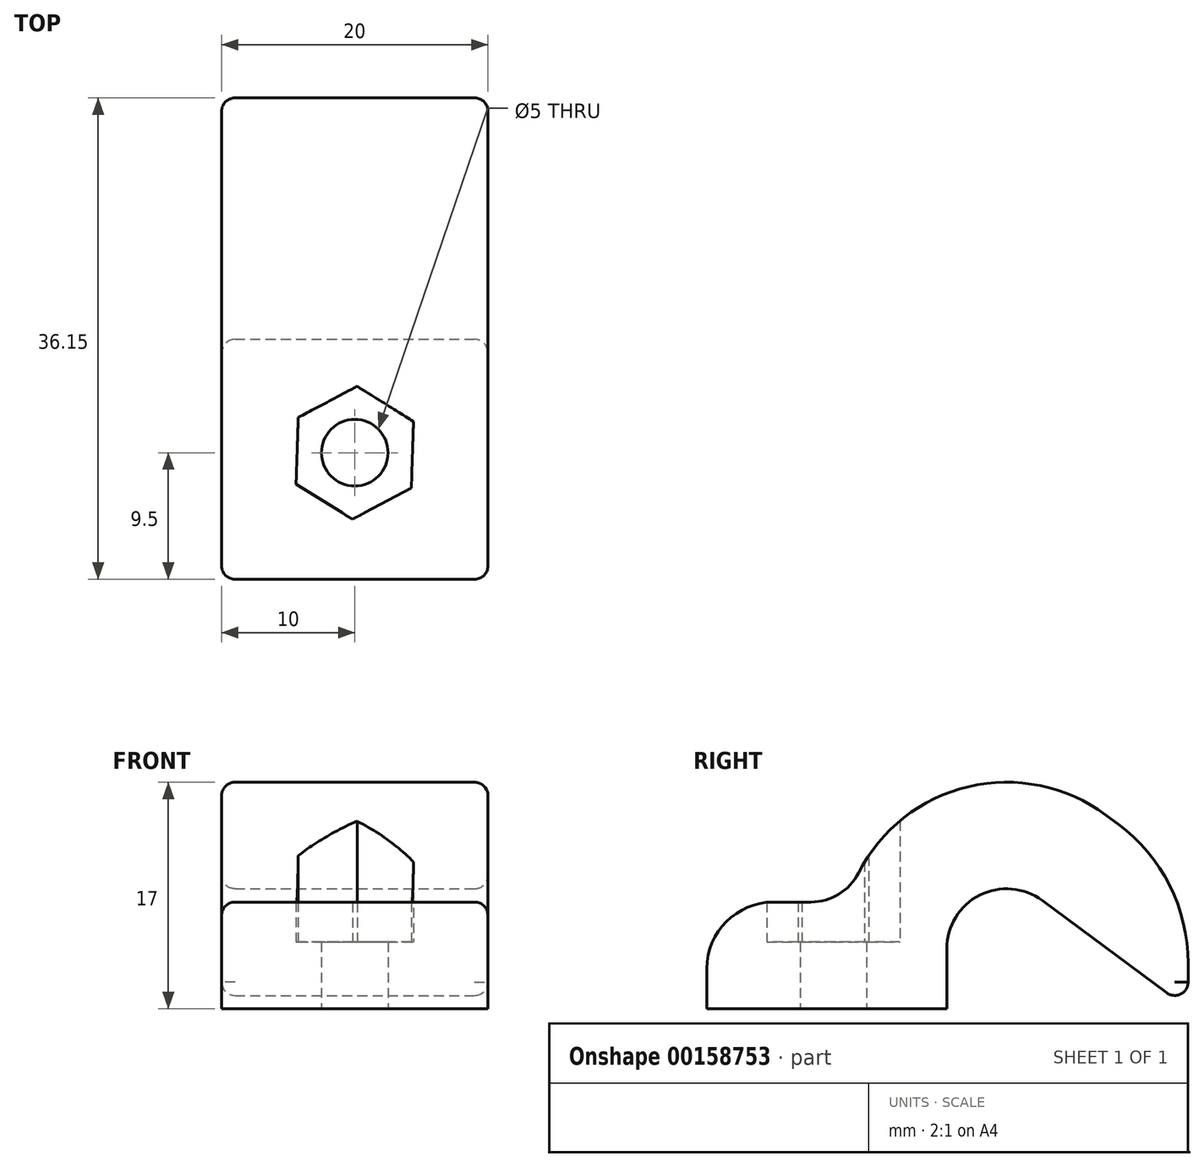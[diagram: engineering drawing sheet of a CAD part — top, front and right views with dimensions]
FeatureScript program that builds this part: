
annotation { "Feature Type Name" : "Feature", "Feature Type Description" : "" }
export const myFeature = defineFeature(function(context is Context, id is Id, definition is map)
    precondition{}
    {
        {
            var Q0;
            Q0=qCreatedBy(makeId("Front.planeOp"),FACE);
            var sketch = newSketch(context, id + "F0", { "sketchPlane" : qUnion([Q0])});
            skArc(sketch, "E0", {"start": v(-18.02, 4.5) * mm, "mid": v(-20.5, 8.52) * mm, "end": v(-25.2, 8.12) * mm});
            skPoint(sketch, "E0.first.point", {"position": v(-22.52, 0) * mm});
            skPoint(sketch, "E0.second.point", {"position": v(-22.52, 9) * mm});
            skPoint(sketch, "E0.third.point", {"position": v(-26.45, 6.68) * mm});
            skLineSegment(sketch, "E1", {"start": v(-36.15, 0) * mm, "end": v(-25.2, 8.12) * mm});
            skLineSegment(sketch, "E2", {"start": v(-18.02, 0) * mm, "end": v(-18.02, 4.5) * mm});
            skLineSegment(sketch, "E3", {"start": v(0, 8) * mm, "end": v(-10.52, 8) * mm});
            skLineSegment(sketch, "E4", {"start": v(-36.15, 9.96) * mm, "end": v(-36.15, 0) * mm});
            skLineSegment(sketch, "E5", {"start": v(0, 8) * mm, "end": v(0, 0) * mm});
            skLineSegment(sketch, "E6", {"start": v(0, 0) * mm, "end": v(-18.02, 0) * mm});
            skPoint(sketch, "E7.start.orphan", {"position": v(0, 16.03) * mm});
            skPoint(sketch, "E8.start.orphan", {"position": v(-36.15, 16.17) * mm});
            skArc(sketch, "E9.1", {"start": v(-10.52, 8) * mm, "mid": v(-18.53, 16.35) * mm, "end": v(-29.96, 14.54) * mm});
            skLineSegment(sketch, "E9.2", {"start": v(-36.15, 9.96) * mm, "end": v(-29.96, 14.54) * mm});
            skPoint(sketch, "E9.0.start.orphan", {"position": v(-10.52, 0) * mm});
            skSolve(sketch);
        }
        {
            var Q0;
            Q0 = qSketchRegion(id + "F0", true);
            extrude(context, id + "F1", {"entities" : qUnion([Q0]), "endBound" : BoundingType.SYMMETRIC, "depth" : 20 * mm});
        }
        {
            var Q0;
            Q0=makeQuery(id+"F1.opExtrude","SWEPT_EDGE",EDGE,{"disambiguationData":[OSD([sQuery(id+"F0.wireOp",EDGE,"E4"),sQuery(id+"F0.wireOp",EDGE,"E9.2")])]});
            fillet(context, id + "F2", {"entities" : qUnion([Q0]), "radius" : 13 * mm, "tangentPropagation" : true, "allowEdgeOverflow" : false});
        }
        {
            var Q0;
            Q0=makeQuery(id+"F1.opExtrude","SWEPT_EDGE",EDGE,{"disambiguationData":[OSD([sQuery(id+"F0.wireOp",EDGE,"E3"),sQuery(id+"F0.wireOp",EDGE,"E9.1")])]});
            fillet(context, id + "F3", {"entities" : qUnion([Q0]), "radius" : 4 * mm, "tangentPropagation" : true, "allowEdgeOverflow" : false});
        }
        {
            var Q0;
            Q0=makeQuery(id+"F1.opExtrude","SWEPT_EDGE",EDGE,{"disambiguationData":[OSD([sQuery(id+"F0.wireOp",EDGE,"E3"),sQuery(id+"F0.wireOp",EDGE,"E5")])]});
            fillet(context, id + "F4", {"entities" : qUnion([Q0]), "radius" : 5 * mm, "tangentPropagation" : true, "allowEdgeOverflow" : false});
        }
        {
            var Q0;
            Q0=makeQuery(id+"F1.opExtrude","SWEPT_FACE",FACE,{"disambiguationData":[OSD([sQuery(id+"F0.wireOp",EDGE,"E6")])]});
            var sketch = newSketch(context, id + "F5", { "sketchPlane" : qUnion([Q0])});
            skCircle(sketch, "E10", {"center": v(-9.5, 0) * mm, "radius": 2.5 * mm});
            skSolve(sketch);
        }
        {
            var Q0;
            Q0 = qSketchRegion(id + "F5", true);
            extrude(context, id + "F6", {"entities" : qUnion([Q0]), "operationType" : NewBodyOperationType.REMOVE, "oppositeDirection" : true, "depth" : 25 * mm});
        }
        {
            var Q0;
            Q0=qCreatedBy(makeId("Top.planeOp"),FACE);
            cPlane(context, id + "F7", {"entities" : qUnion([Q0]), "cplaneType" : CPlaneType.OFFSET, "offset" : 5 * mm, "width" : 150 * mm, "height" : 150 * mm});
        }
        {
            var Q0;
            Q0=makeQuery(id+"F1.opExtrude","SWEPT_BODY",BODY,{"disambiguationData":[OSD([sQuery(id+"F0.wireOp",EDGE,"E0"),sQuery(id+"F0.wireOp",EDGE,"E1"),sQuery(id+"F0.wireOp",EDGE,"E2"),sQuery(id+"F0.wireOp",EDGE,"E3"),sQuery(id+"F0.wireOp",EDGE,"E4"),sQuery(id+"F0.wireOp",EDGE,"E5"),sQuery(id+"F0.wireOp",EDGE,"E6"),sQuery(id+"F0.wireOp",EDGE,"E9.1"),sQuery(id+"F0.wireOp",EDGE,"E9.2")])]});
            var Q1;
            Q1=makeQuery(id+"F1.opExtrude","CAP_EDGE",EDGE,{"disambiguationData":[OSD([sQuery(id+"F0.wireOp",EDGE,"E5")])],"isStart":false});
            transform(context, id + "F8", {"entities" : qUnion([Q0]), "transformType" : TransformType.ROTATION, "transformAxis" : qUnion([Q1]), "angle" : 90 * degree, "makeCopy" : false});
        }
        {
            var Q0;
            Q0=qCreatedBy(id+"F7.planeOp",FACE);
            var sketch = newSketch(context, id + "F9", { "sketchPlane" : qUnion([Q0])});
            skCircle(sketch, "E11.cCircle", {"center": v(10, -0.5) * mm, "radius": 5 * mm, "construction": true});
            skLineSegment(sketch, "E11.0", {"start": v(14.41, 1.85) * mm, "end": v(14.24, -3.15) * mm});
            skLineSegment(sketch, "E11.1", {"start": v(14.24, -3.15) * mm, "end": v(9.83, -5.5) * mm});
            skLineSegment(sketch, "E11.2", {"start": v(9.83, -5.5) * mm, "end": v(5.59, -2.85) * mm});
            skLineSegment(sketch, "E11.3", {"start": v(5.59, -2.85) * mm, "end": v(5.76, 2.15) * mm});
            skLineSegment(sketch, "E11.4", {"start": v(5.76, 2.15) * mm, "end": v(10.17, 4.5) * mm});
            skLineSegment(sketch, "E11.5", {"start": v(10.17, 4.5) * mm, "end": v(14.41, 1.85) * mm});
            skSolve(sketch);
        }
        {
            var Q0;
            Q0 = qSketchRegion(id + "F9", true);
            extrude(context, id + "F10", {"entities" : qUnion([Q0]), "operationType" : NewBodyOperationType.REMOVE, "depth" : 25 * mm});
        }
        {
            var Q0;
            Q0=makeQuery(id+"F1.opExtrude","CAP_EDGE",EDGE,{"disambiguationData":[OSD([sQuery(id+"F0.wireOp",EDGE,"E9.1")])],"isStart":false});
            var Q1;
            Q1=makeQuery(id+"F1.opExtrude","CAP_EDGE",EDGE,{"disambiguationData":[OSD([sQuery(id+"F0.wireOp",EDGE,"E9.2")])],"isStart":false});
            var Q2;
            {var subQ0=sQuery(id+"F0.wireOp",EDGE,"E9.2");var subQ1=sQuery(id+"F0.wireOp",EDGE,"E4");Q2=makeQuery(id+"F2.opFillet","BLEND_EDGE",EDGE,{"blendedFrom":[makeQuery(id+"F1.opExtrude","SWEPT_EDGE",EDGE,{"disambiguationData":[OSD([subQ1,subQ0])]}),makeQuery(id+"F1.opExtrude","CAP_FACE",FACE,{"disambiguationData":[OSD([sQuery(id+"F0.wireOp",EDGE,"E0"),sQuery(id+"F0.wireOp",EDGE,"E1"),sQuery(id+"F0.wireOp",EDGE,"E2"),sQuery(id+"F0.wireOp",EDGE,"E3"),subQ1,sQuery(id+"F0.wireOp",EDGE,"E5"),sQuery(id+"F0.wireOp",EDGE,"E6"),sQuery(id+"F0.wireOp",EDGE,"E9.1"),subQ0])],"isStart":false})],"blendedInto":[makeQuery(id+"F1.opExtrude","CAP_FACE",FACE,{"disambiguationData":[OSD([sQuery(id+"F0.wireOp",EDGE,"E0"),sQuery(id+"F0.wireOp",EDGE,"E1"),sQuery(id+"F0.wireOp",EDGE,"E2"),sQuery(id+"F0.wireOp",EDGE,"E3"),subQ1,sQuery(id+"F0.wireOp",EDGE,"E5"),sQuery(id+"F0.wireOp",EDGE,"E6"),sQuery(id+"F0.wireOp",EDGE,"E9.1"),subQ0])],"isStart":false})]});}
            var Q3;
            {var subQ0=sQuery(id+"F0.wireOp",EDGE,"E9.1");var subQ1=sQuery(id+"F0.wireOp",EDGE,"E3");Q3=makeQuery(id+"F3.opFillet","BLEND_EDGE",EDGE,{"blendedFrom":[makeQuery(id+"F1.opExtrude","SWEPT_EDGE",EDGE,{"disambiguationData":[OSD([subQ1,subQ0])]}),makeQuery(id+"F1.opExtrude","CAP_FACE",FACE,{"disambiguationData":[OSD([sQuery(id+"F0.wireOp",EDGE,"E0"),sQuery(id+"F0.wireOp",EDGE,"E1"),sQuery(id+"F0.wireOp",EDGE,"E2"),subQ1,sQuery(id+"F0.wireOp",EDGE,"E4"),sQuery(id+"F0.wireOp",EDGE,"E5"),sQuery(id+"F0.wireOp",EDGE,"E6"),subQ0,sQuery(id+"F0.wireOp",EDGE,"E9.2")])],"isStart":false})],"blendedInto":[makeQuery(id+"F1.opExtrude","CAP_FACE",FACE,{"disambiguationData":[OSD([sQuery(id+"F0.wireOp",EDGE,"E0"),sQuery(id+"F0.wireOp",EDGE,"E1"),sQuery(id+"F0.wireOp",EDGE,"E2"),subQ1,sQuery(id+"F0.wireOp",EDGE,"E4"),sQuery(id+"F0.wireOp",EDGE,"E5"),sQuery(id+"F0.wireOp",EDGE,"E6"),subQ0,sQuery(id+"F0.wireOp",EDGE,"E9.2")])],"isStart":false})]});}
            var Q4;
            Q4=makeQuery(id+"F1.opExtrude","CAP_EDGE",EDGE,{"disambiguationData":[OSD([sQuery(id+"F0.wireOp",EDGE,"E3")])],"isStart":false});
            var Q5;
            {var subQ0=sQuery(id+"F0.wireOp",EDGE,"E5");var subQ1=sQuery(id+"F0.wireOp",EDGE,"E3");Q5=makeQuery(id+"F4.opFillet","BLEND_EDGE",EDGE,{"blendedFrom":[makeQuery(id+"F1.opExtrude","SWEPT_EDGE",EDGE,{"disambiguationData":[OSD([subQ1,subQ0])]}),makeQuery(id+"F1.opExtrude","CAP_FACE",FACE,{"disambiguationData":[OSD([sQuery(id+"F0.wireOp",EDGE,"E0"),sQuery(id+"F0.wireOp",EDGE,"E1"),sQuery(id+"F0.wireOp",EDGE,"E2"),subQ1,sQuery(id+"F0.wireOp",EDGE,"E4"),subQ0,sQuery(id+"F0.wireOp",EDGE,"E6"),sQuery(id+"F0.wireOp",EDGE,"E9.1"),sQuery(id+"F0.wireOp",EDGE,"E9.2")])],"isStart":false})],"blendedInto":[makeQuery(id+"F1.opExtrude","CAP_FACE",FACE,{"disambiguationData":[OSD([sQuery(id+"F0.wireOp",EDGE,"E0"),sQuery(id+"F0.wireOp",EDGE,"E1"),sQuery(id+"F0.wireOp",EDGE,"E2"),subQ1,sQuery(id+"F0.wireOp",EDGE,"E4"),subQ0,sQuery(id+"F0.wireOp",EDGE,"E6"),sQuery(id+"F0.wireOp",EDGE,"E9.1"),sQuery(id+"F0.wireOp",EDGE,"E9.2")])],"isStart":false})]});}
            var Q6;
            Q6=makeQuery(id+"F1.opExtrude","CAP_EDGE",EDGE,{"disambiguationData":[OSD([sQuery(id+"F0.wireOp",EDGE,"E5")])],"isStart":false});
            var Q7;
            Q7=makeQuery(id+"F1.opExtrude","CAP_EDGE",EDGE,{"disambiguationData":[OSD([sQuery(id+"F0.wireOp",EDGE,"E4")])],"isStart":false});
            var Q8;
            Q8=makeQuery(id+"F1.opExtrude","CAP_EDGE",EDGE,{"disambiguationData":[OSD([sQuery(id+"F0.wireOp",EDGE,"E9.1")])],"isStart":true});
            var Q9;
            {var subQ0=sQuery(id+"F0.wireOp",EDGE,"E9.1");var subQ1=sQuery(id+"F0.wireOp",EDGE,"E3");Q9=makeQuery(id+"F3.opFillet","BLEND_EDGE",EDGE,{"blendedFrom":[makeQuery(id+"F1.opExtrude","SWEPT_EDGE",EDGE,{"disambiguationData":[OSD([subQ1,subQ0])]}),makeQuery(id+"F1.opExtrude","CAP_FACE",FACE,{"disambiguationData":[OSD([sQuery(id+"F0.wireOp",EDGE,"E0"),sQuery(id+"F0.wireOp",EDGE,"E1"),sQuery(id+"F0.wireOp",EDGE,"E2"),subQ1,sQuery(id+"F0.wireOp",EDGE,"E4"),sQuery(id+"F0.wireOp",EDGE,"E5"),sQuery(id+"F0.wireOp",EDGE,"E6"),subQ0,sQuery(id+"F0.wireOp",EDGE,"E9.2")])],"isStart":true})],"blendedInto":[makeQuery(id+"F1.opExtrude","CAP_FACE",FACE,{"disambiguationData":[OSD([sQuery(id+"F0.wireOp",EDGE,"E0"),sQuery(id+"F0.wireOp",EDGE,"E1"),sQuery(id+"F0.wireOp",EDGE,"E2"),subQ1,sQuery(id+"F0.wireOp",EDGE,"E4"),sQuery(id+"F0.wireOp",EDGE,"E5"),sQuery(id+"F0.wireOp",EDGE,"E6"),subQ0,sQuery(id+"F0.wireOp",EDGE,"E9.2")])],"isStart":true})]});}
            var Q10;
            Q10=makeQuery(id+"F1.opExtrude","CAP_EDGE",EDGE,{"disambiguationData":[OSD([sQuery(id+"F0.wireOp",EDGE,"E3")])],"isStart":true});
            var Q11;
            {var subQ0=sQuery(id+"F0.wireOp",EDGE,"E5");var subQ1=sQuery(id+"F0.wireOp",EDGE,"E3");Q11=makeQuery(id+"F4.opFillet","BLEND_EDGE",EDGE,{"blendedFrom":[makeQuery(id+"F1.opExtrude","SWEPT_EDGE",EDGE,{"disambiguationData":[OSD([subQ1,subQ0])]}),makeQuery(id+"F1.opExtrude","CAP_FACE",FACE,{"disambiguationData":[OSD([sQuery(id+"F0.wireOp",EDGE,"E0"),sQuery(id+"F0.wireOp",EDGE,"E1"),sQuery(id+"F0.wireOp",EDGE,"E2"),subQ1,sQuery(id+"F0.wireOp",EDGE,"E4"),subQ0,sQuery(id+"F0.wireOp",EDGE,"E6"),sQuery(id+"F0.wireOp",EDGE,"E9.1"),sQuery(id+"F0.wireOp",EDGE,"E9.2")])],"isStart":true})],"blendedInto":[makeQuery(id+"F1.opExtrude","CAP_FACE",FACE,{"disambiguationData":[OSD([sQuery(id+"F0.wireOp",EDGE,"E0"),sQuery(id+"F0.wireOp",EDGE,"E1"),sQuery(id+"F0.wireOp",EDGE,"E2"),subQ1,sQuery(id+"F0.wireOp",EDGE,"E4"),subQ0,sQuery(id+"F0.wireOp",EDGE,"E6"),sQuery(id+"F0.wireOp",EDGE,"E9.1"),sQuery(id+"F0.wireOp",EDGE,"E9.2")])],"isStart":true})]});}
            var Q12;
            Q12=makeQuery(id+"F1.opExtrude","CAP_EDGE",EDGE,{"disambiguationData":[OSD([sQuery(id+"F0.wireOp",EDGE,"E5")])],"isStart":true});
            var Q13;
            Q13=makeQuery(id+"F1.opExtrude","CAP_EDGE",EDGE,{"disambiguationData":[OSD([sQuery(id+"F0.wireOp",EDGE,"E9.2")])],"isStart":true});
            var Q14;
            {var subQ0=sQuery(id+"F0.wireOp",EDGE,"E9.2");var subQ1=sQuery(id+"F0.wireOp",EDGE,"E4");Q14=makeQuery(id+"F2.opFillet","BLEND_EDGE",EDGE,{"blendedFrom":[makeQuery(id+"F1.opExtrude","SWEPT_EDGE",EDGE,{"disambiguationData":[OSD([subQ1,subQ0])]}),makeQuery(id+"F1.opExtrude","CAP_FACE",FACE,{"disambiguationData":[OSD([sQuery(id+"F0.wireOp",EDGE,"E0"),sQuery(id+"F0.wireOp",EDGE,"E1"),sQuery(id+"F0.wireOp",EDGE,"E2"),sQuery(id+"F0.wireOp",EDGE,"E3"),subQ1,sQuery(id+"F0.wireOp",EDGE,"E5"),sQuery(id+"F0.wireOp",EDGE,"E6"),sQuery(id+"F0.wireOp",EDGE,"E9.1"),subQ0])],"isStart":true})],"blendedInto":[makeQuery(id+"F1.opExtrude","CAP_FACE",FACE,{"disambiguationData":[OSD([sQuery(id+"F0.wireOp",EDGE,"E0"),sQuery(id+"F0.wireOp",EDGE,"E1"),sQuery(id+"F0.wireOp",EDGE,"E2"),sQuery(id+"F0.wireOp",EDGE,"E3"),subQ1,sQuery(id+"F0.wireOp",EDGE,"E5"),sQuery(id+"F0.wireOp",EDGE,"E6"),sQuery(id+"F0.wireOp",EDGE,"E9.1"),subQ0])],"isStart":true})]});}
            var Q15;
            Q15=makeQuery(id+"F1.opExtrude","CAP_EDGE",EDGE,{"disambiguationData":[OSD([sQuery(id+"F0.wireOp",EDGE,"E4")])],"isStart":true});
            fillet(context, id + "F11", {"entities" : qUnion([Q0, Q1, Q2, Q3, Q4, Q5, Q6, Q7, Q8, Q9, Q10, Q11, Q12, Q13, Q14, Q15]), "radius" : 1 * mm, "tangentPropagation" : true, "allowEdgeOverflow" : false});
        }
        {
            var Q0;
            Q0=makeQuery(id+"F1.opExtrude","SWEPT_EDGE",EDGE,{"disambiguationData":[OSD([sQuery(id+"F0.wireOp",EDGE,"E1"),sQuery(id+"F0.wireOp",EDGE,"E4")])]});
            fillet(context, id + "F12", {"entities" : qUnion([Q0]), "radius" : 1 * mm, "tangentPropagation" : true, "allowEdgeOverflow" : false});
        }
    });
